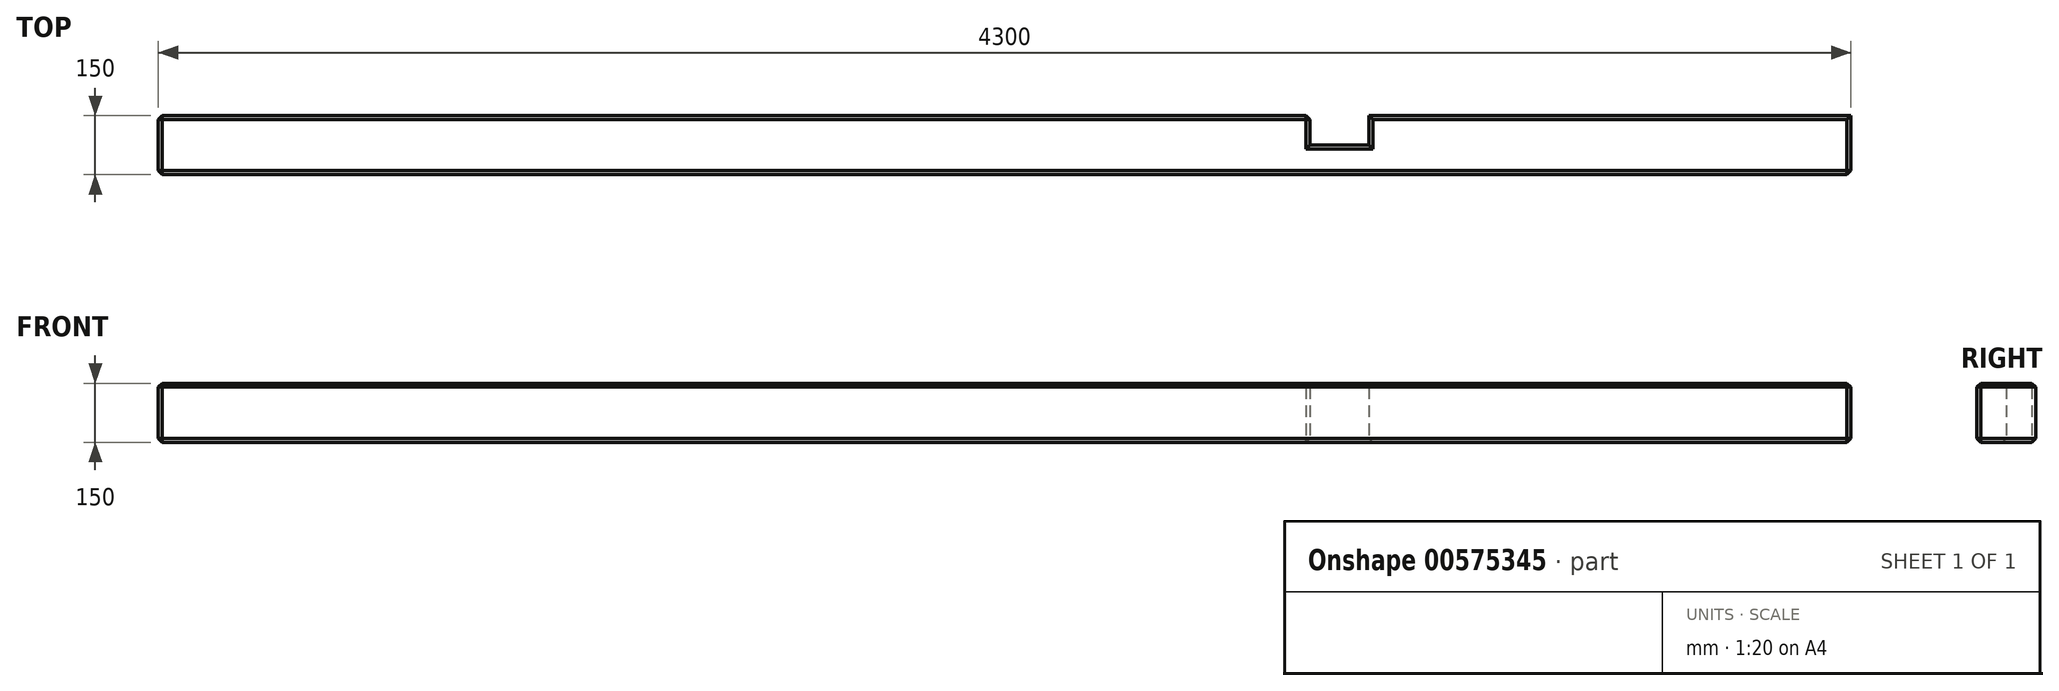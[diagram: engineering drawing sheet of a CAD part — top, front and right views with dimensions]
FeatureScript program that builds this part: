
annotation { "Feature Type Name" : "Feature", "Feature Type Description" : "" }
export const myFeature = defineFeature(function(context is Context, id is Id, definition is map)
    precondition{}
    {
        {
            var Q0;
            Q0=qCreatedBy(makeId("Top.planeOp"),FACE);
            var sketch = newSketch(context, id + "F0", { "sketchPlane" : qUnion([Q0])});
            skLineSegment(sketch, "E0.bottom", {"start": v(-2150, 75) * mm, "end": v(775, 75) * mm});
            skLineSegment(sketch, "E0.top", {"start": v(-2150, -75) * mm, "end": v(2150, -75) * mm});
            skLineSegment(sketch, "E0.left", {"start": v(-2150, 75) * mm, "end": v(-2150, -75) * mm});
            skLineSegment(sketch, "E0.right", {"start": v(2150, 75) * mm, "end": v(2150, -75) * mm});
            skPoint(sketch, "E0.middle", {"position": v(0, 0) * mm});
            skLineSegment(sketch, "E1", {"start": v(775, 75) * mm, "end": v(775, 0) * mm});
            skLineSegment(sketch, "E2", {"start": v(925, 0) * mm, "end": v(925, 75) * mm});
            skLineSegment(sketch, "E3.trimOffspring", {"start": v(925, 75) * mm, "end": v(2150, 75) * mm});
            skLineSegment(sketch, "E4", {"start": v(775, 0) * mm, "end": v(925, 0) * mm});
            skSolve(sketch);
        }
        {
            var Q0;
            Q0=makeQuery(id+"F0.imprint","IMPRINT",FACE,{"disambiguationData":[TD([[makeQuery(id+"F0.imprint","IMPRINT",EDGE,{"derivedFrom":sQuery(id+"F0.wireOp",EDGE,"E0.bottom")}),-1.0]])]});
            extrude(context, id + "F1", {"entities" : qUnion([Q0]), "depth" : 150 * mm});
        }
        {
            var Q0;
            Q0=makeQuery(id+"F1.opExtrude","CAP_FACE",FACE,{"disambiguationData":[OSD([sQuery(id+"F0.wireOp",EDGE,"E0.bottom"),sQuery(id+"F0.wireOp",EDGE,"E0.top"),sQuery(id+"F0.wireOp",EDGE,"E0.left"),sQuery(id+"F0.wireOp",EDGE,"E0.right")])],"isStart":false});
            var Q1;
            Q1=makeQuery(id+"F1.opExtrude","SWEPT_FACE",FACE,{"disambiguationData":[OSD([sQuery(id+"F0.wireOp",EDGE,"E0.top")])]});
            var Q2;
            Q2=makeQuery(id+"F1.opExtrude","CAP_FACE",FACE,{"disambiguationData":[OSD([sQuery(id+"F0.wireOp",EDGE,"E0.bottom"),sQuery(id+"F0.wireOp",EDGE,"E0.top"),sQuery(id+"F0.wireOp",EDGE,"E0.left"),sQuery(id+"F0.wireOp",EDGE,"E0.right")])],"isStart":true});
            var Q3;
            Q3=makeQuery(id+"F1.opExtrude","SWEPT_FACE",FACE,{"disambiguationData":[OSD([sQuery(id+"F0.wireOp",EDGE,"E0.bottom")])]});
            chamfer(context, id + "F2", {"entities" : qUnion([Q0, Q1, Q2, Q3]), "width" : 10 * mm, "tangentPropagation" : true});
        }
    });
